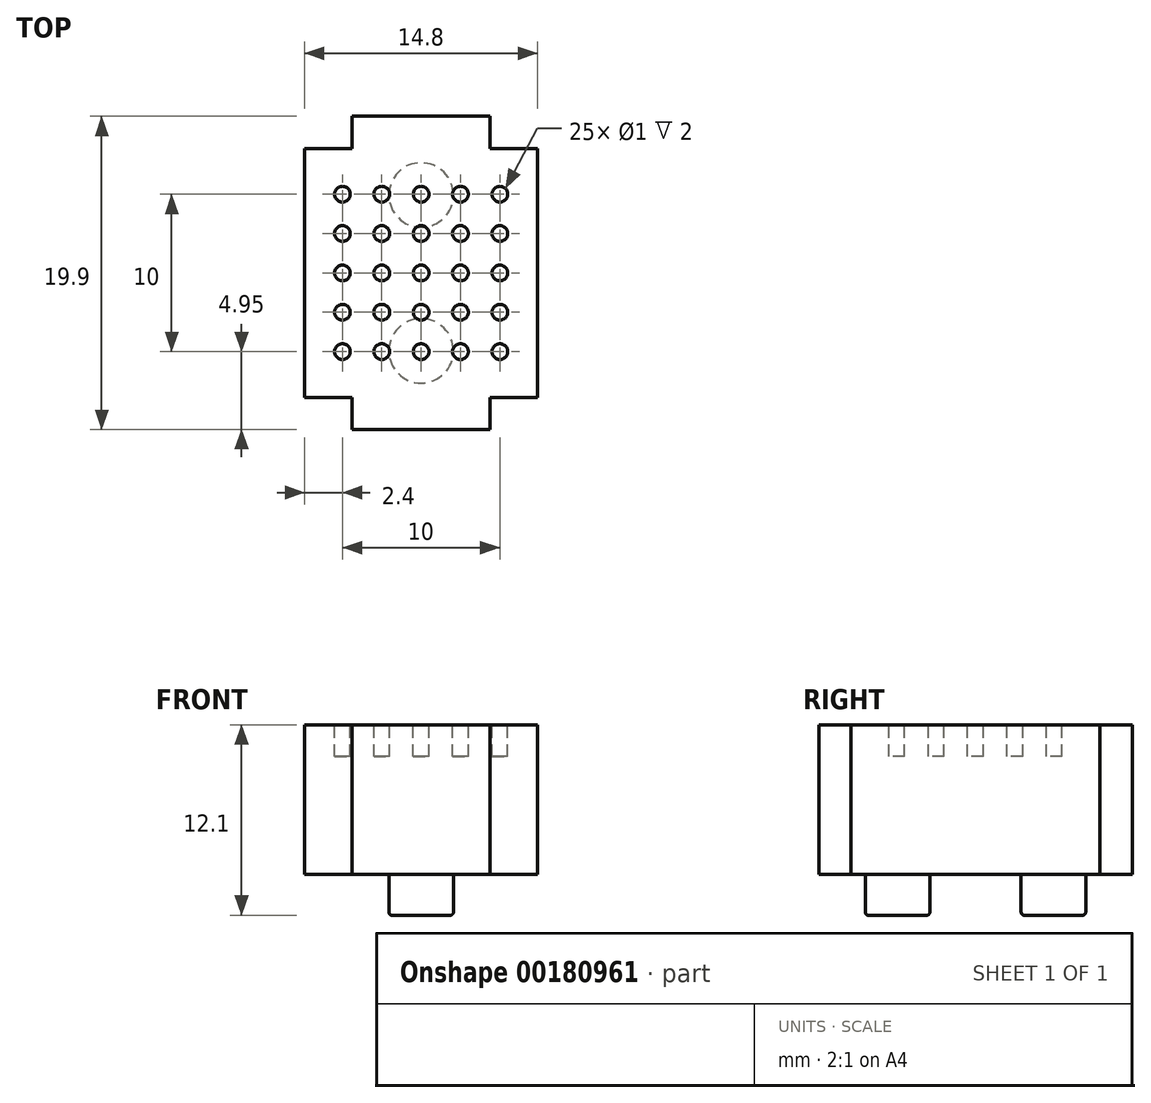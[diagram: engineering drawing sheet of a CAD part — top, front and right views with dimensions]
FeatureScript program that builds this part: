
annotation { "Feature Type Name" : "Feature", "Feature Type Description" : "" }
export const myFeature = defineFeature(function(context is Context, id is Id, definition is map)
    precondition{}
    {
        {
            var Q0;
            Q0=qCreatedBy(makeId("Top.planeOp"),FACE);
            var sketch = newSketch(context, id + "F0", { "sketchPlane" : qUnion([Q0])});
            skLineSegment(sketch, "E0", {"start": v(-9.95, 0) * mm, "end": v(-9.95, 4.37) * mm});
            skLineSegment(sketch, "E1", {"start": v(-9.95, 4.38) * mm, "end": v(-7.9, 4.38) * mm});
            skLineSegment(sketch, "E2", {"start": v(-7.9, 4.37) * mm, "end": v(-7.9, 7.4) * mm});
            skLineSegment(sketch, "E3", {"start": v(-7.9, 7.4) * mm, "end": v(0, 7.4) * mm});
            skLineSegment(sketch, "E4", {"start": v(0, 7.4) * mm, "end": v(0, 0) * mm, "construction": true});
            skLineSegment(sketch, "E5", {"start": v(0, 0) * mm, "end": v(-9.95, 0) * mm, "construction": true});
            skLineSegment(sketch, "E6.MirrorCS", {"start": v(-7.9, -7.4) * mm, "end": v(0, -7.4) * mm});
            skLineSegment(sketch, "E7.MirrorCS", {"start": v(-7.9, -4.37) * mm, "end": v(-7.9, -7.4) * mm});
            skLineSegment(sketch, "E8.MirrorCS", {"start": v(-9.95, -4.37) * mm, "end": v(-7.9, -4.37) * mm});
            skLineSegment(sketch, "E9.MirrorCS", {"start": v(-9.95, 0) * mm, "end": v(-9.95, -4.38) * mm});
            skLineSegment(sketch, "E10.MirrorCS", {"start": v(7.9, 7.4) * mm, "end": v(0, 7.4) * mm});
            skLineSegment(sketch, "E11.MirrorCS", {"start": v(7.9, 4.38) * mm, "end": v(7.9, 7.4) * mm});
            skLineSegment(sketch, "E12.MirrorCS", {"start": v(9.95, 0) * mm, "end": v(9.95, 4.38) * mm});
            skLineSegment(sketch, "E13.MirrorCS", {"start": v(9.95, 0) * mm, "end": v(9.95, -4.37) * mm});
            skLineSegment(sketch, "E14.MirrorCS", {"start": v(9.95, -4.38) * mm, "end": v(7.9, -4.38) * mm});
            skLineSegment(sketch, "E15.MirrorCS", {"start": v(7.9, -7.4) * mm, "end": v(0, -7.4) * mm});
            skLineSegment(sketch, "E16.MirrorCS", {"start": v(7.9, -4.37) * mm, "end": v(7.9, -7.4) * mm});
            skLineSegment(sketch, "E17.MirrorCS", {"start": v(9.95, 4.38) * mm, "end": v(7.9, 4.38) * mm});
            skSolve(sketch);
        }
        {
            var Q0;
            Q0 = qSketchRegion(id + "F0", true);
            extrude(context, id + "F1", {"entities" : qUnion([Q0]), "depth" : 9.5 * mm});
        }
        {
            var Q0;
            Q0=makeQuery(id+"F1.opExtrude","CAP_FACE",FACE,{"disambiguationData":[OSD([sQuery(id+"F0.wireOp",EDGE,"E0"),sQuery(id+"F0.wireOp",EDGE,"E1"),sQuery(id+"F0.wireOp",EDGE,"E2"),sQuery(id+"F0.wireOp",EDGE,"E3"),sQuery(id+"F0.wireOp",EDGE,"E6.MirrorCS"),sQuery(id+"F0.wireOp",EDGE,"E7.MirrorCS"),sQuery(id+"F0.wireOp",EDGE,"E8.MirrorCS"),sQuery(id+"F0.wireOp",EDGE,"E9.MirrorCS"),sQuery(id+"F0.wireOp",EDGE,"E10.MirrorCS"),sQuery(id+"F0.wireOp",EDGE,"E12.MirrorCS"),sQuery(id+"F0.wireOp",EDGE,"E13.MirrorCS"),sQuery(id+"F0.wireOp",EDGE,"E14.MirrorCS"),sQuery(id+"F0.wireOp",EDGE,"E15.MirrorCS"),sQuery(id+"F0.wireOp",EDGE,"E16.MirrorCS"),sQuery(id+"F0.wireOp",EDGE,"E11.MirrorCS"),sQuery(id+"F0.wireOp",EDGE,"E17.MirrorCS")])],"isStart":false});
            var sketch = newSketch(context, id + "F2", { "sketchPlane" : qUnion([Q0])});
            skCircle(sketch, "E18", {"center": v(0, 0) * mm, "radius": 0.5 * mm});
            skCircle(sketch, "E19.0.1.0", {"center": v(0, 2.5) * mm, "radius": 0.5 * mm});
            skCircle(sketch, "E19.0.2.0", {"center": v(0, 5) * mm, "radius": 0.5 * mm});
            skCircle(sketch, "E19.1.0.0", {"center": v(2.5, 0) * mm, "radius": 0.5 * mm});
            skCircle(sketch, "E19.1.1.0", {"center": v(2.5, 2.5) * mm, "radius": 0.5 * mm});
            skCircle(sketch, "E19.1.2.0", {"center": v(2.5, 5) * mm, "radius": 0.5 * mm});
            skCircle(sketch, "E19.2.0.0", {"center": v(5, 0) * mm, "radius": 0.5 * mm});
            skCircle(sketch, "E19.2.1.0", {"center": v(5, 2.5) * mm, "radius": 0.5 * mm});
            skCircle(sketch, "E19.2.2.0", {"center": v(5, 5) * mm, "radius": 0.5 * mm});
            skLineSegment(sketch, "E19.direction1", {"start": v(0, 0) * mm, "end": v(2.5, 0) * mm, "construction": true});
            skLineSegment(sketch, "E19.direction2", {"start": v(0, 0) * mm, "end": v(0, 2.5) * mm, "construction": true});
            skCircle(sketch, "E20.MirrorC", {"center": v(-5, 0) * mm, "radius": 0.5 * mm});
            skCircle(sketch, "E21.MirrorC", {"center": v(-2.5, 5) * mm, "radius": 0.5 * mm});
            skCircle(sketch, "E22.MirrorC", {"center": v(-2.5, 2.5) * mm, "radius": 0.5 * mm});
            skCircle(sketch, "E23.MirrorC", {"center": v(-2.5, 0) * mm, "radius": 0.5 * mm});
            skCircle(sketch, "E24.MirrorC", {"center": v(-5, 2.5) * mm, "radius": 0.5 * mm});
            skCircle(sketch, "E25.MirrorC", {"center": v(-5, 5) * mm, "radius": 0.5 * mm});
            skCircle(sketch, "E26.MirrorC", {"center": v(2.5, -5) * mm, "radius": 0.5 * mm});
            skCircle(sketch, "E27.MirrorC", {"center": v(2.5, -2.5) * mm, "radius": 0.5 * mm});
            skCircle(sketch, "E28.MirrorC", {"center": v(0, -5) * mm, "radius": 0.5 * mm});
            skCircle(sketch, "E29.MirrorC", {"center": v(0, -2.5) * mm, "radius": 0.5 * mm});
            skCircle(sketch, "E30.MirrorC", {"center": v(-5, -2.5) * mm, "radius": 0.5 * mm});
            skCircle(sketch, "E31.MirrorC", {"center": v(5, -2.5) * mm, "radius": 0.5 * mm});
            skCircle(sketch, "E32.MirrorC", {"center": v(5, -5) * mm, "radius": 0.5 * mm});
            skCircle(sketch, "E33.MirrorC", {"center": v(-2.5, -5) * mm, "radius": 0.5 * mm});
            skCircle(sketch, "E34.MirrorC", {"center": v(-5, -5) * mm, "radius": 0.5 * mm});
            skCircle(sketch, "E35.MirrorC", {"center": v(-2.5, -2.5) * mm, "radius": 0.5 * mm});
            skSolve(sketch);
        }
        {
            var Q0;
            Q0 = qSketchRegion(id + "F2", true);
            extrude(context, id + "F3", {"entities" : qUnion([Q0]), "operationType" : NewBodyOperationType.REMOVE, "oppositeDirection" : true, "depth" : 2 * mm});
        }
        {
            var Q0;
            Q0=qCreatedBy(makeId("Top.planeOp"),FACE);
            var sketch = newSketch(context, id + "F4", { "sketchPlane" : qUnion([Q0])});
            skCircle(sketch, "E36", {"center": v(-4.95, 0) * mm, "radius": 2.05 * mm});
            skCircle(sketch, "E37.MirrorC", {"center": v(4.95, 0) * mm, "radius": 2.05 * mm});
            skSolve(sketch);
        }
        {
            var Q0;
            Q0 = qSketchRegion(id + "F4", true);
            extrude(context, id + "F5", {"entities" : qUnion([Q0]), "operationType" : NewBodyOperationType.ADD, "oppositeDirection" : true, "depth" : 2.6 * mm});
        }
        {
            var Q0;
            Q0=makeQuery(id+"F5.opExtrude","CAP_FACE",FACE,{"disambiguationData":[OSD([sQuery(id+"F4.wireOp",EDGE,"E36")])],"isStart":false});
            var Q1;
            Q1=makeQuery(id+"F5.opExtrude","CAP_FACE",FACE,{"disambiguationData":[OSD([sQuery(id+"F4.wireOp",EDGE,"E37.MirrorC")])],"isStart":false});
            fillet(context, id + "F6", {"entities" : qUnion([Q0, Q1]), "radius" : 0.2 * mm, "tangentPropagation" : true, "allowEdgeOverflow" : false});
        }
        {
            var Q0;
            Q0=qCreatedBy(makeId("Front.planeOp"),FACE);
            var sketch = newSketch(context, id + "F7", { "sketchPlane" : qUnion([Q0])});
            skLineSegment(sketch, "E38", {"start": v(0, 0) * mm, "end": v(0, 67.8) * mm, "construction": true});
            skSolve(sketch);
        }
        {
            var Q0;
            Q0=makeQuery(id+"F1.opExtrude","SWEPT_BODY",BODY,{"disambiguationData":[OSD([sQuery(id+"F0.wireOp",EDGE,"E0"),sQuery(id+"F0.wireOp",EDGE,"E1"),sQuery(id+"F0.wireOp",EDGE,"E2"),sQuery(id+"F0.wireOp",EDGE,"E3"),sQuery(id+"F0.wireOp",EDGE,"E6.MirrorCS"),sQuery(id+"F0.wireOp",EDGE,"E7.MirrorCS"),sQuery(id+"F0.wireOp",EDGE,"E8.MirrorCS"),sQuery(id+"F0.wireOp",EDGE,"E9.MirrorCS"),sQuery(id+"F0.wireOp",EDGE,"E10.MirrorCS"),sQuery(id+"F0.wireOp",EDGE,"E12.MirrorCS"),sQuery(id+"F0.wireOp",EDGE,"E13.MirrorCS"),sQuery(id+"F0.wireOp",EDGE,"E14.MirrorCS"),sQuery(id+"F0.wireOp",EDGE,"E15.MirrorCS"),sQuery(id+"F0.wireOp",EDGE,"E16.MirrorCS"),sQuery(id+"F0.wireOp",EDGE,"E11.MirrorCS"),sQuery(id+"F0.wireOp",EDGE,"E17.MirrorCS")])]});
            var Q1;
            Q1=sQuery(id+"F7.wireOp",EDGE,"E38");
            transform(context, id + "F8", {"entities" : qUnion([Q0]), "transformType" : TransformType.ROTATION, "transformAxis" : qUnion([Q1]), "angle" : 90 * degree, "makeCopy" : false});
        }
    });
